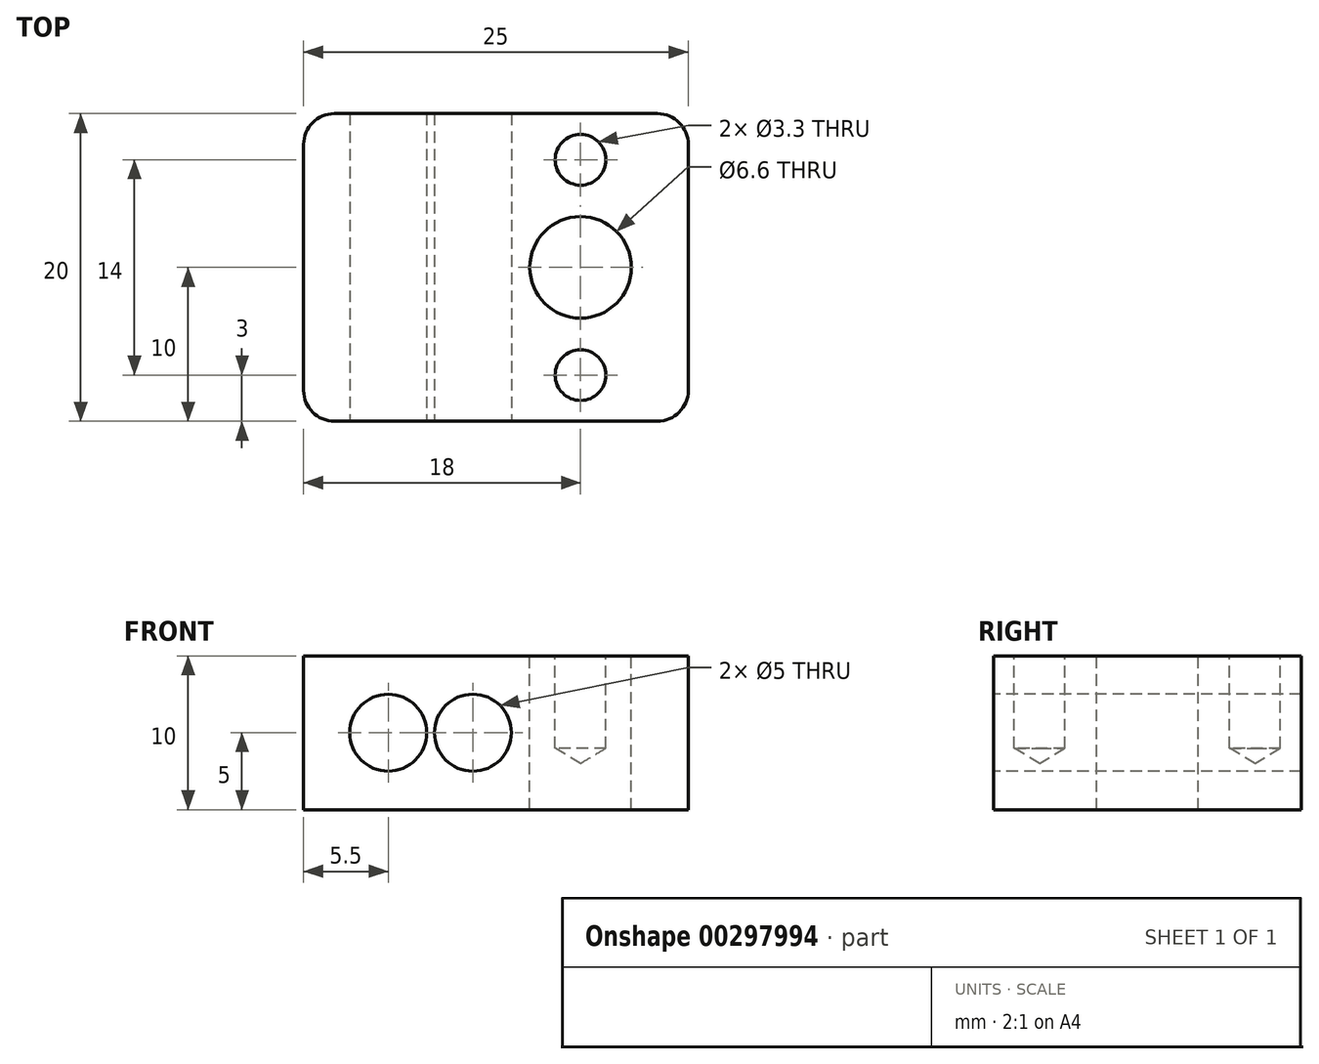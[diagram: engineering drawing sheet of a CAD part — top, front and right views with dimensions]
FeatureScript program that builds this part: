
annotation { "Feature Type Name" : "Feature", "Feature Type Description" : "" }
export const myFeature = defineFeature(function(context is Context, id is Id, definition is map)
    precondition{}
    {
        {
            var Q0;
            Q0=qCreatedBy(makeId("Top.planeOp"),FACE);
            var sketch = newSketch(context, id + "F0", { "sketchPlane" : qUnion([Q0])});
            skLineSegment(sketch, "E0.bottom", {"start": v(12.5, 10) * mm, "end": v(-12.5, 10) * mm});
            skLineSegment(sketch, "E0.top", {"start": v(12.5, -10) * mm, "end": v(-12.5, -10) * mm});
            skLineSegment(sketch, "E0.left", {"start": v(12.5, 10) * mm, "end": v(12.5, -10) * mm});
            skLineSegment(sketch, "E0.right", {"start": v(-12.5, 10) * mm, "end": v(-12.5, -10) * mm});
            skPoint(sketch, "E0.middle", {"position": v(0, 0) * mm});
            skSolve(sketch);
        }
        {
            var Q0;
            Q0=makeQuery(id+"F0.imprint","IMPRINT",FACE,{"disambiguationData":[TD([[makeQuery(id+"F0.imprint","IMPRINT",EDGE,{"derivedFrom":sQuery(id+"F0.wireOp",EDGE,"E0.bottom")}),1.0]])]});
            extrude(context, id + "F1", {"entities" : qUnion([Q0]), "depth" : 10 * mm});
        }
        {
            var Q0;
            Q0=makeQuery(id+"F1.opExtrude","CAP_FACE",FACE,{"disambiguationData":[OSD([sQuery(id+"F0.wireOp",EDGE,"E0.bottom"),sQuery(id+"F0.wireOp",EDGE,"E0.top"),sQuery(id+"F0.wireOp",EDGE,"E0.left"),sQuery(id+"F0.wireOp",EDGE,"E0.right")])],"isStart":false});
            var sketch = newSketch(context, id + "F2", { "sketchPlane" : qUnion([Q0])});
            skLineSegment(sketch, "E1.0", {"start": v(12.5, 10) * mm, "end": v(12.5, -10) * mm});
            skPoint(sketch, "E2", {"position": v(5.5, 0) * mm});
            skSolve(sketch);
        }
        {
            var Q0;
            Q0=sQuery(id+"F2.wireOp",VERTEX,"E2");
            var Q1;
            Q1=makeQuery(id+"F1.opExtrude","SWEPT_BODY",BODY,{"disambiguationData":[OSD([sQuery(id+"F0.wireOp",EDGE,"E0.bottom"),sQuery(id+"F0.wireOp",EDGE,"E0.top"),sQuery(id+"F0.wireOp",EDGE,"E0.left"),sQuery(id+"F0.wireOp",EDGE,"E0.right")])]});
            hole(context, id + "F3", {"style" : HoleStyle.SIMPLE, "endStyle" : HoleEndStyle.BLIND, "standardTappedOrClearance" : lookupTablePath({ "standard" : "ISO", "fit" : "Normal", "size" : "M6", "type" : "Clearance" }), "standardBlindInLast" : lookupTablePath({ "fit" : "Standard", "standard" : "ISO", "size" : "M6", "type" : "Clearance" }), "holeDiameter" : 6.6 * mm, "holeDepth" : 10 * mm, "tappedDepth" : 12 * mm, "tapClearance" : 3, "locations" : qUnion([Q0]), "scope" : qUnion([Q1])});
        }
        {
            var Q0;
            Q0=makeQuery(id+"F1.opExtrude","SWEPT_FACE",FACE,{"disambiguationData":[OSD([sQuery(id+"F0.wireOp",EDGE,"E0.top")])]});
            var sketch = newSketch(context, id + "F4", { "sketchPlane" : qUnion([Q0])});
            skLineSegment(sketch, "E3.0", {"start": v(-12.5, 10) * mm, "end": v(-12.5, 0) * mm});
            skPoint(sketch, "E4", {"position": v(-7, 5) * mm});
            skPoint(sketch, "E4.positionSnap0", {"position": v(-12.5, 5) * mm});
            skPoint(sketch, "E5", {"position": v(-1.5, 5) * mm});
            skSolve(sketch);
        }
        {
            var Q0;
            Q0=sQuery(id+"F4.wireOp",VERTEX,"E4");
            var Q1;
            Q1=sQuery(id+"F4.wireOp",VERTEX,"E5");
            var Q2;
            Q2=makeQuery(id+"F1.opExtrude","SWEPT_BODY",BODY,{"disambiguationData":[OSD([sQuery(id+"F0.wireOp",EDGE,"E0.bottom"),sQuery(id+"F0.wireOp",EDGE,"E0.top"),sQuery(id+"F0.wireOp",EDGE,"E0.left"),sQuery(id+"F0.wireOp",EDGE,"E0.right")])]});
            hole(context, id + "F5", {"style" : HoleStyle.SIMPLE, "endStyle" : HoleEndStyle.BLIND, "holeDiameter" : 5 * mm, "holeDepth" : 30 * mm, "tappedDepth" : 12 * mm, "tapClearance" : 3, "locations" : qUnion([Q0, Q1]), "scope" : qUnion([Q2])});
        }
        {
            var Q0;
            Q0=makeQuery(id+"F1.opExtrude","SWEPT_EDGE",EDGE,{"disambiguationData":[OSD([sQuery(id+"F0.wireOp",EDGE,"E0.top"),sQuery(id+"F0.wireOp",EDGE,"E0.right")])]});
            var Q1;
            Q1=makeQuery(id+"F1.opExtrude","SWEPT_EDGE",EDGE,{"disambiguationData":[OSD([sQuery(id+"F0.wireOp",EDGE,"E0.bottom"),sQuery(id+"F0.wireOp",EDGE,"E0.right")])]});
            var Q2;
            Q2=makeQuery(id+"F1.opExtrude","SWEPT_EDGE",EDGE,{"disambiguationData":[OSD([sQuery(id+"F0.wireOp",EDGE,"E0.top"),sQuery(id+"F0.wireOp",EDGE,"E0.left")])]});
            var Q3;
            Q3=makeQuery(id+"F1.opExtrude","SWEPT_EDGE",EDGE,{"disambiguationData":[OSD([sQuery(id+"F0.wireOp",EDGE,"E0.bottom"),sQuery(id+"F0.wireOp",EDGE,"E0.left")])]});
            fillet(context, id + "F6", {"entities" : qUnion([Q0, Q1, Q2, Q3]), "radius" : 2 * mm, "tangentPropagation" : true, "allowEdgeOverflow" : false});
        }
        {
            var Q0;
            Q0=makeQuery(id+"F1.opExtrude","CAP_FACE",FACE,{"disambiguationData":[OSD([sQuery(id+"F0.wireOp",EDGE,"E0.bottom"),sQuery(id+"F0.wireOp",EDGE,"E0.top"),sQuery(id+"F0.wireOp",EDGE,"E0.left"),sQuery(id+"F0.wireOp",EDGE,"E0.right")])],"isStart":false});
            var sketch = newSketch(context, id + "F7", { "sketchPlane" : qUnion([Q0])});
            skPoint(sketch, "E6", {"position": v(5.5, -7) * mm});
            skPoint(sketch, "E7", {"position": v(5.5, 7) * mm});
            skSolve(sketch);
        }
        {
            var Q0;
            Q0=sQuery(id+"F7.wireOp",VERTEX,"E7");
            var Q1;
            Q1=sQuery(id+"F7.wireOp",VERTEX,"E6");
            var Q2;
            Q2=makeQuery(id+"F1.opExtrude","SWEPT_BODY",BODY,{"disambiguationData":[OSD([sQuery(id+"F0.wireOp",EDGE,"E0.bottom"),sQuery(id+"F0.wireOp",EDGE,"E0.top"),sQuery(id+"F0.wireOp",EDGE,"E0.left"),sQuery(id+"F0.wireOp",EDGE,"E0.right")])]});
            hole(context, id + "F8", {"style" : HoleStyle.SIMPLE, "endStyle" : HoleEndStyle.BLIND, "standardTappedOrClearance" : lookupTablePath({ "standard" : "ISO", "fit" : "Normal", "size" : "M3", "type" : "Clearance" }), "standardBlindInLast" : lookupTablePath({ "fit" : "Standard", "standard" : "ISO", "size" : "M3", "type" : "Clearance" }), "holeDiameter" : 3.3 * mm, "holeDepth" : 6 * mm, "tappedDepth" : 12 * mm, "tapClearance" : 3, "locations" : qUnion([Q0, Q1]), "scope" : qUnion([Q2])});
        }
    });
